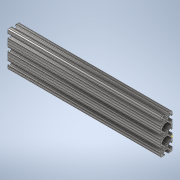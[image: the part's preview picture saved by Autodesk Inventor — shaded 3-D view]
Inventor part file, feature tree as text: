
AUTODESK INVENTOR PART (.ipt)
format: ipt  version: 2020 (Build 240168000, 168)  size: 378,368 bytes
history: native  units: in
note: dims shown in document units (in); Inventor stores cm internally (conversion verified against a paired STEP export)
features: sketch x2, extrude x1
ambient origin geometry x8: Origin, YZ Plane, XZ Plane, XY Plane, X Axis, Y Axis, Z Axis, Center Point
bodies: Solid1 (feature_tree)
feature tree (3):
  extrude  "Extrusion1"  [1 undecoded]
  sketch  "Sketch2"
  sketch  "Sketch1"  dims[d0=13.0in d1=0.0in]
note: 1 required parameter value undecoded (feature->parameter linkage not recoverable at this tier; creation-order binding heuristic only, values carry confidence <= 0.55)
